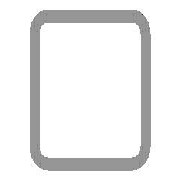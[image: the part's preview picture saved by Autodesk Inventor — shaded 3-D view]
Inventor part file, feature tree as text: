
AUTODESK INVENTOR PART (.ipt)
format: ipt  version: 2025 (Build 290162010, 162A)  size: 134,656 bytes
history: native  units: mm (DEFAULTED — no unit token found)
features: other x4, sketch x1, plane x1
ambient origin geometry x8: Origin, YZ Plane, XZ Plane, XY Plane, X Axis, Y Axis, Z Axis, Center Point
bodies: Solid1 (feature_tree), Body (feature_tree)
feature tree (6):
  parser-record x1  (decoder bookkeeping rows leaked as tree rows — omitted from the tree; the rows remain in map.json)
  other  "Driven Length"
  other  "Start Plane"
  other  "End Plane"
  sketch  "Sketch3"  dims[d3=1580.0mm d4=0.0mm d7=6.0mm d9=80.0mm d11=80.0mm d12=3.0mm d13=80.0mm d14=1660.0mm d15=40.0mm d16=40.0mm d17=90.0deg d18=1580.0mm]
  plane  "Work Plane3"
